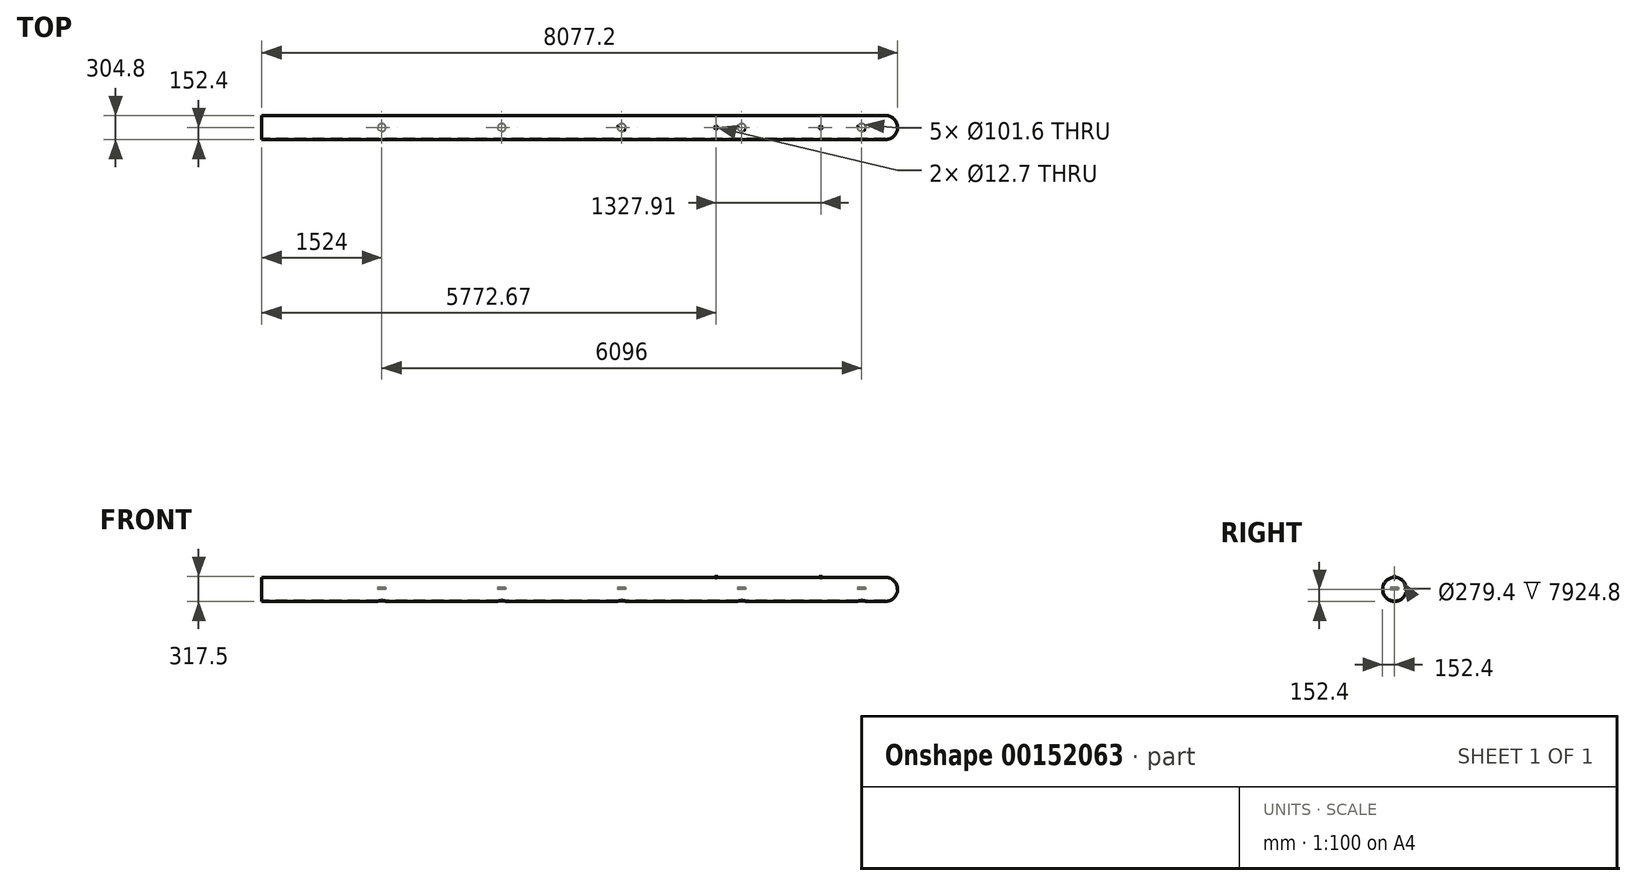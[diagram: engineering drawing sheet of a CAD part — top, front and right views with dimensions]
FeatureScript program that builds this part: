
annotation { "Feature Type Name" : "Feature", "Feature Type Description" : "" }
export const myFeature = defineFeature(function(context is Context, id is Id, definition is map)
    precondition{}
    {
        {
            var Q0;
            Q0=qCreatedBy(makeId("Front.planeOp"),FACE);
            var sketch = newSketch(context, id + "F0", { "sketchPlane" : qUnion([Q0])});
            skLineSegment(sketch, "E0.bottom", {"start": v(0, 0) * mm, "end": v(8077.2, 0) * mm});
            skLineSegment(sketch, "E0.top", {"start": v(0, 152.4) * mm, "end": v(7924.8, 152.4) * mm});
            skLineSegment(sketch, "E0.left", {"start": v(0, 0) * mm, "end": v(0, 152.4) * mm});
            skLineSegment(sketch, "E1", {"start": v(8077.2, 0) * mm, "end": v(7924.8, 0) * mm});
            skArc(sketch, "E2", {"start": v(8077.2, 0) * mm, "mid": v(8032.56, 107.76) * mm, "end": v(7924.8, 152.4) * mm});
            skSolve(sketch);
        }
        {
            var Q0;
            Q0 = qSketchRegion(id + "F0", true);
            var Q1;
            Q1=sQuery(id+"F0.wireOp",EDGE,"E0.bottom");
            revolve(context, id + "F1", {"entities" : qUnion([Q0]), "axis" : qUnion([Q1]), "revolveType" : RevolveType.FULL});
        }
        {
            var Q0;
            Q0=makeQuery(id+"F1.opRevolve","SWEPT_FACE",FACE,{"disambiguationData":[OSD([sQuery(id+"F0.wireOp",EDGE,"E0.left")])]});
            shell(context, id + "F2", {"entities" : qUnion([Q0]), "thickness" : 12.7 * mm});
        }
        {
            var Q0;
            Q0=qCreatedBy(makeId("Top.planeOp"),FACE);
            var sketch = newSketch(context, id + "F3", { "sketchPlane" : qUnion([Q0])});
            skCircle(sketch, "E3", {"center": v(7620, 0) * mm, "radius": 50.8 * mm});
            skCircle(sketch, "E4", {"center": v(6096, 0) * mm, "radius": 50.8 * mm});
            skCircle(sketch, "E5", {"center": v(4572, 0) * mm, "radius": 50.8 * mm});
            skCircle(sketch, "E6", {"center": v(3048, 0) * mm, "radius": 50.8 * mm});
            skCircle(sketch, "E7", {"center": v(1524, 0) * mm, "radius": 50.8 * mm});
            skSolve(sketch);
        }
        {
            var Q0;
            Q0 = qSketchRegion(id + "F3", true);
            extrude(context, id + "F4", {"entities" : qUnion([Q0]), "operationType" : NewBodyOperationType.REMOVE, "oppositeDirection" : true, "depth" : 254 * mm});
        }
        {
            var Q0;
            Q0 = qSketchRegion(id + "F3", true);
            extrude(context, id + "F5", {"entities" : qUnion([Q0]), "depth" : 25.4 * mm});
        }
        {
            var Q0;
            Q0=qCreatedBy(makeId("Top.planeOp"),FACE);
            var sketch = newSketch(context, id + "F6", { "sketchPlane" : qUnion([Q0])});
            skCircle(sketch, "E8", {"center": v(7100.44, 0) * mm, "radius": 12.7 * mm});
            skCircle(sketch, "E9", {"center": v(5773.12, 0) * mm, "radius": 12.7 * mm});
            skSolve(sketch);
        }
        {
            var Q0;
            Q0 = qSketchRegion(id + "F6", true);
            extrude(context, id + "F7", {"entities" : qUnion([Q0]), "operationType" : NewBodyOperationType.REMOVE, "depth" : 304.8 * mm});
        }
        {
            var Q0;
            Q0=qCreatedBy(makeId("Top.planeOp"),FACE);
            cPlane(context, id + "F8", {"entities" : qUnion([Q0]), "cplaneType" : CPlaneType.OFFSET, "offset" : 152.4 * mm, "width" : 152.4 * mm, "height" : 152.4 * mm});
        }
        {
            var Q0;
            Q0=qCreatedBy(id+"F8.planeOp",FACE);
            var sketch = newSketch(context, id + "F9", { "sketchPlane" : qUnion([Q0])});
            skCircle(sketch, "E10", {"center": v(5772.67, 0) * mm, "radius": 15.1 * mm});
            skCircle(sketch, "E11", {"center": v(5772.67, 0) * mm, "radius": 6.35 * mm});
            skCircle(sketch, "E12", {"center": v(7100.58, 0) * mm, "radius": 14.36 * mm});
            skCircle(sketch, "E13", {"center": v(7100.58, 0) * mm, "radius": 6.35 * mm});
            skSolve(sketch);
        }
        {
            var Q0;
            Q0 = qSketchRegion(id + "F9", true);
            extrude(context, id + "F10", {"entities" : qUnion([Q0]), "operationType" : NewBodyOperationType.ADD, "depth" : 25.4 * mm, "symmetric" : true});
        }
        {
            var Q0;
            Q0=makeQuery(id+"F10.boolean.opBoolean","INTERSECT",EDGE,{"derivedFrom":[makeQuery(id+"F1.opRevolve","SWEPT_FACE",FACE,{"disambiguationData":[OSD([sQuery(id+"F0.wireOp",EDGE,"E0.top")])]}),makeQuery(id+"F10.opExtrude","SWEPT_FACE",FACE,{"disambiguationData":[OSD([sQuery(id+"F9.wireOp",EDGE,"E12")])]})]});
            fillet(context, id + "F11", {"entities" : qUnion([Q0]), "radius" : 5.08 * mm, "tangentPropagation" : true, "allowEdgeOverflow" : false});
        }
        {
            var Q0;
            Q0=makeQuery(id+"F10.opExtrude","CAP_EDGE",EDGE,{"disambiguationData":[OSD([sQuery(id+"F9.wireOp",EDGE,"E12")])],"isStart":false});
            var Q1;
            Q1=makeQuery(id+"F10.opExtrude","CAP_EDGE",EDGE,{"disambiguationData":[OSD([sQuery(id+"F9.wireOp",EDGE,"E10")])],"isStart":false});
            chamfer(context, id + "F12", {"entities" : qUnion([Q0, Q1]), "width" : 1.27 * mm, "tangentPropagation" : true});
        }
        {
            var Q0;
            Q0=makeQuery(id+"F10.boolean.opBoolean","INTERSECT",EDGE,{"derivedFrom":[makeQuery(id+"F1.opRevolve","SWEPT_FACE",FACE,{"disambiguationData":[OSD([sQuery(id+"F0.wireOp",EDGE,"E0.top")])]}),makeQuery(id+"F10.opExtrude","SWEPT_FACE",FACE,{"disambiguationData":[OSD([sQuery(id+"F9.wireOp",EDGE,"E10")])]})]});
            fillet(context, id + "F13", {"entities" : qUnion([Q0]), "radius" : 5.08 * mm, "tangentPropagation" : true, "allowEdgeOverflow" : false});
        }
    });
